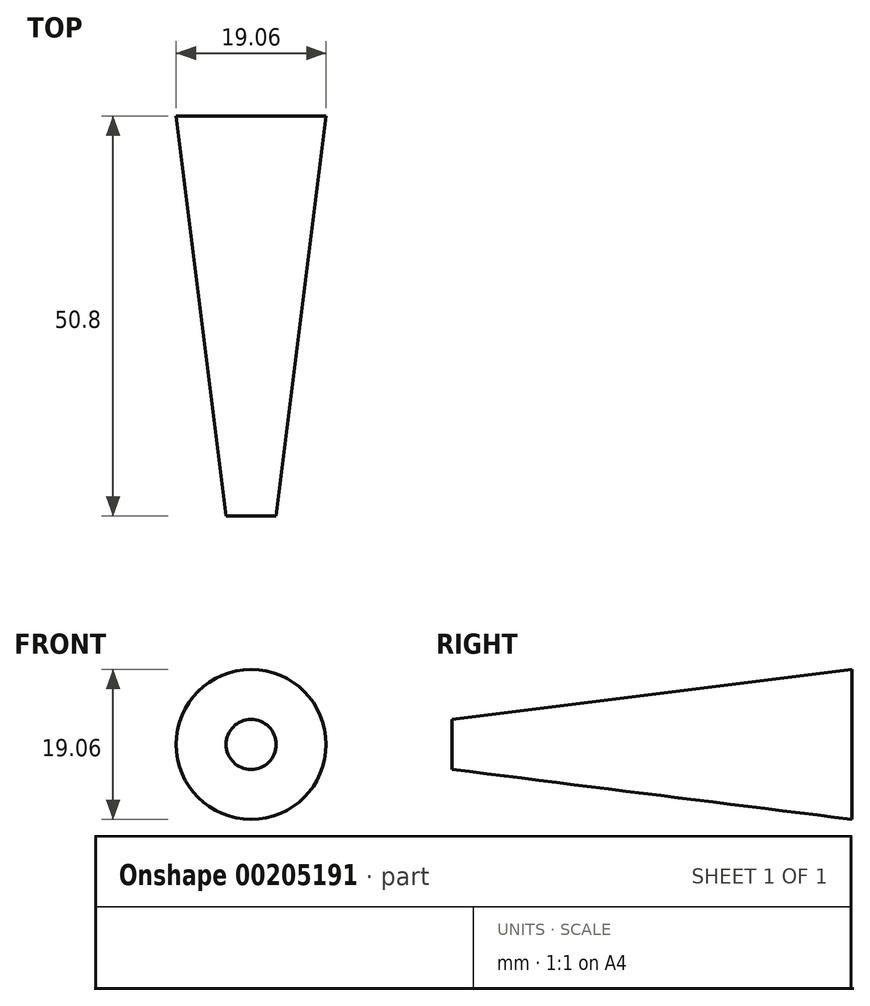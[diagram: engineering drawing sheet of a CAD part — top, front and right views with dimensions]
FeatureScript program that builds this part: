
annotation { "Feature Type Name" : "Feature", "Feature Type Description" : "" }
export const myFeature = defineFeature(function(context is Context, id is Id, definition is map)
    precondition{}
    {
        {
            var Q0;
            Q0=qCreatedBy(makeId("Front.planeOp"),FACE);
            var sketch = newSketch(context, id + "F0", { "sketchPlane" : qUnion([Q0])});
            skCircle(sketch, "E0", {"center": v(0, 0) * mm, "radius": 9.53 * mm});
            skSolve(sketch);
        }
        {
            var Q0;
            Q0=qCreatedBy(makeId("Front.planeOp"),FACE);
            cPlane(context, id + "F1", {"entities" : qUnion([Q0]), "cplaneType" : CPlaneType.OFFSET, "offset" : 50.8 * mm, "width" : 152.4 * mm, "height" : 152.4 * mm});
        }
        {
            var Q0;
            Q0=qCreatedBy(id+"F1.planeOp",FACE);
            var sketch = newSketch(context, id + "F2", { "sketchPlane" : qUnion([Q0])});
            skCircle(sketch, "E1", {"center": v(0, 0) * mm, "radius": 3.18 * mm});
            skSolve(sketch);
        }
        {
            var Q0;
            Q0=makeQuery(id+"F2.imprint","IMPRINT",FACE,{"disambiguationData":[TD([[makeQuery(id+"F2.imprint","IMPRINT",EDGE,{"derivedFrom":sQuery(id+"F2.wireOp",EDGE,"E1")}),1.0]])]});
            var Q1;
            Q1=makeQuery(id+"F0.imprint","IMPRINT",FACE,{"disambiguationData":[TD([[makeQuery(id+"F0.imprint","IMPRINT",EDGE,{"derivedFrom":sQuery(id+"F0.wireOp",EDGE,"E0")}),1.0]])]});
            loft(context, id + "F3", {"sheetProfilesArray" : [{ "sheetProfileEntities" : qUnion([Q0]) }, { "sheetProfileEntities" : qUnion([Q1]) }]});
        }
    });
